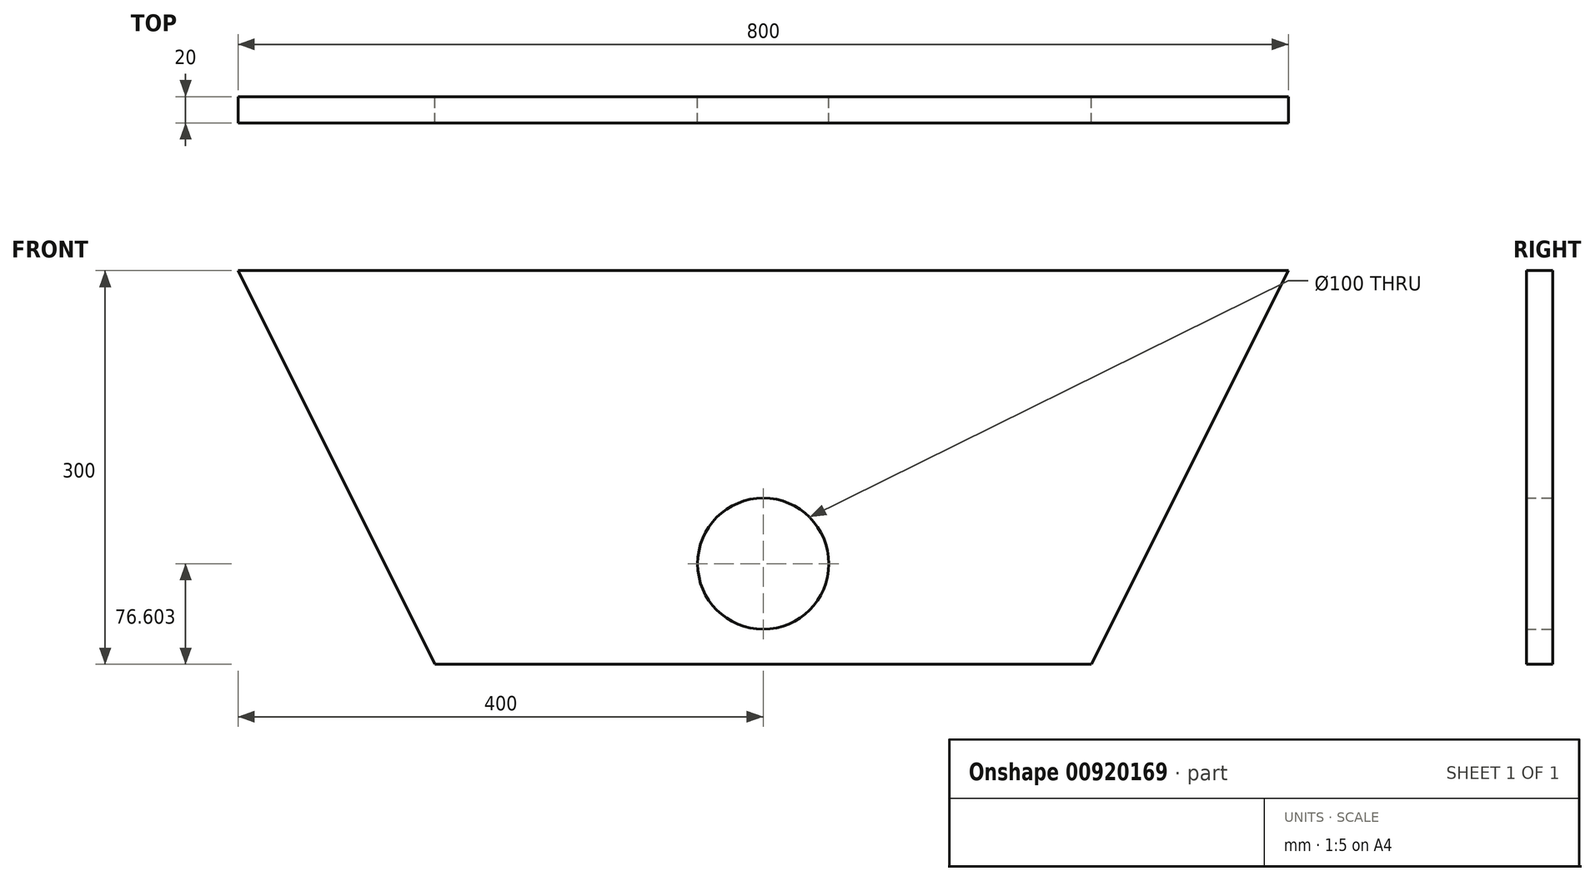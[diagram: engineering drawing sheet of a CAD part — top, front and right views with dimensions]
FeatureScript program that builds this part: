
annotation { "Feature Type Name" : "Feature", "Feature Type Description" : "" }
export const myFeature = defineFeature(function(context is Context, id is Id, definition is map)
    precondition{}
    {
        {
            var Q0;
            Q0=qCreatedBy(makeId("Front.planeOp"),FACE);
            var sketch = newSketch(context, id + "F0", { "sketchPlane" : qUnion([Q0])});
            skLineSegment(sketch, "E0", {"start": v(-250, -214.06) * mm, "end": v(250, -214.06) * mm});
            skLineSegment(sketch, "E1", {"start": v(399.2, 84.34) * mm, "end": v(250, -214.06) * mm});
            skLineSegment(sketch, "E2", {"start": v(-399.2, 84.34) * mm, "end": v(-250, -214.06) * mm});
            skLineSegment(sketch, "E3", {"start": v(-400, 85.94) * mm, "end": v(-399.2, 84.34) * mm});
            skLineSegment(sketch, "E4", {"start": v(399.2, 84.34) * mm, "end": v(400, 85.94) * mm});
            skLineSegment(sketch, "E5", {"start": v(400, 85.94) * mm, "end": v(-400, 85.94) * mm});
            skCircle(sketch, "E6", {"center": v(0, -137.46) * mm, "radius": 50 * mm});
            skPoint(sketch, "E7.start.orphan", {"position": v(0, -214.06) * mm});
            skSolve(sketch);
        }
        {
            var Q0;
            Q0=qSketchRegion(id+"F0",true);
            extrude(context, id + "F1", {"entities" : qUnion([Q0]), "depth" : 20 * mm, "offsetDistance" : 25 * mm});
        }
    });
